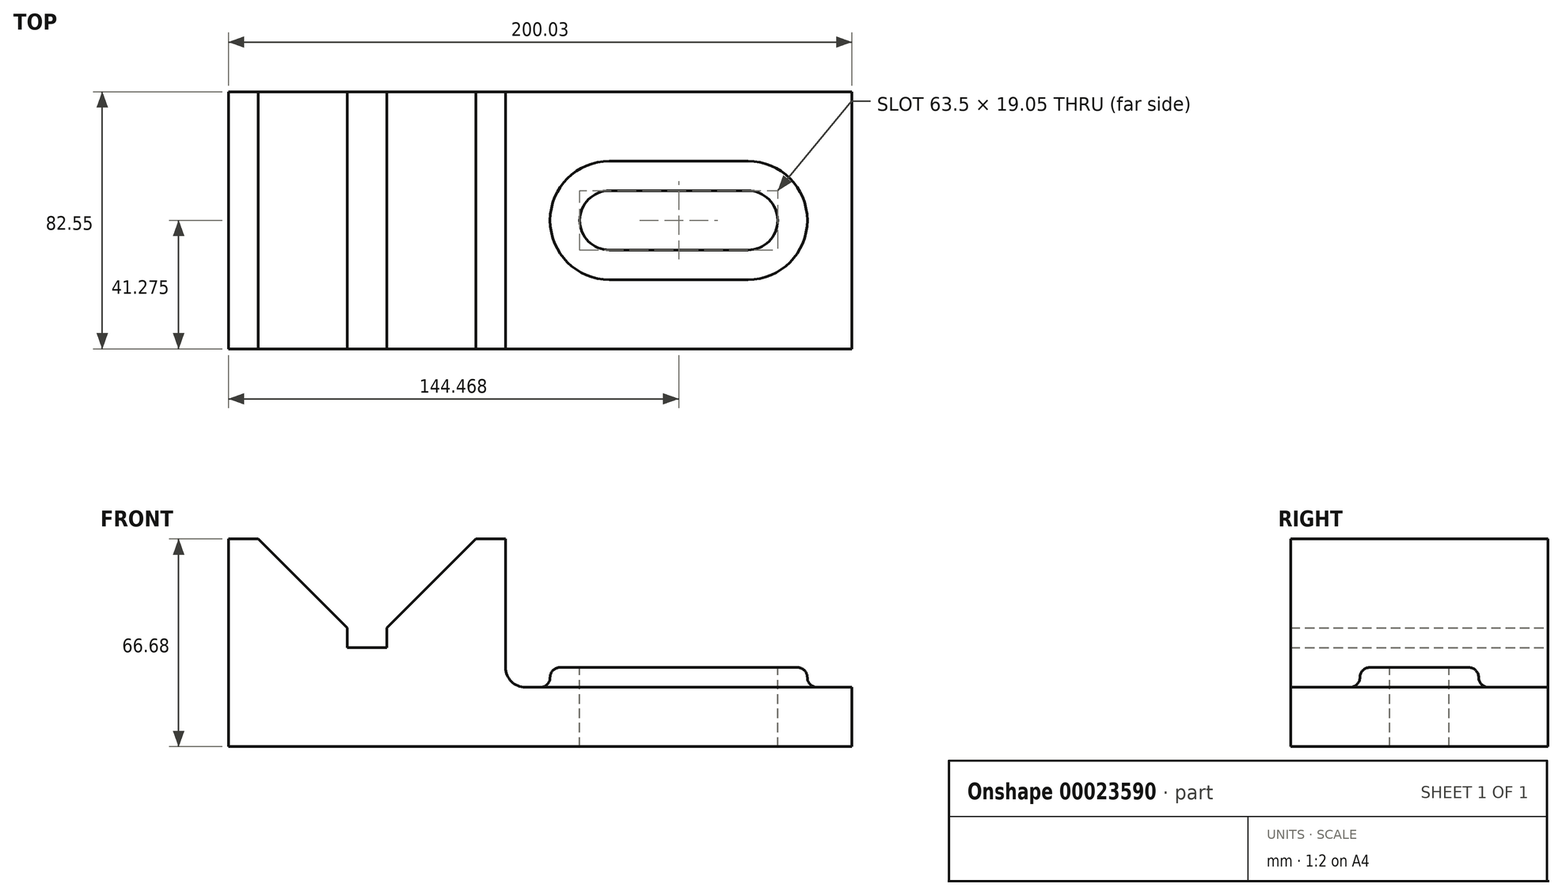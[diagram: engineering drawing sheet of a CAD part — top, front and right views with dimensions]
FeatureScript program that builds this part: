
annotation { "Feature Type Name" : "Feature", "Feature Type Description" : "" }
export const myFeature = defineFeature(function(context is Context, id is Id, definition is map)
    precondition{}
    {
        {
            var Q0;
            Q0=qCreatedBy(makeId("Front.planeOp"),FACE);
            var sketch = newSketch(context, id + "F0", { "sketchPlane" : qUnion([Q0])});
            skLineSegment(sketch, "E0.bottom", {"start": v(-200.03, 19.05) * mm, "end": v(0, 19.05) * mm});
            skLineSegment(sketch, "E0.top", {"start": v(-200.03, 0) * mm, "end": v(0, 0) * mm});
            skLineSegment(sketch, "E0.left", {"start": v(-200.03, 19.05) * mm, "end": v(-200.03, 0) * mm});
            skLineSegment(sketch, "E0.right", {"start": v(0, 19.05) * mm, "end": v(0, 0) * mm});
            skLineSegment(sketch, "E1.bottom", {"start": v(-200.03, 0) * mm, "end": v(-111.13, 0) * mm});
            skLineSegment(sketch, "E1.top", {"start": v(-200.03, 66.68) * mm, "end": v(-111.13, 66.68) * mm});
            skLineSegment(sketch, "E1.left", {"start": v(-200.03, 0) * mm, "end": v(-200.03, 66.68) * mm});
            skLineSegment(sketch, "E1.right", {"start": v(-111.13, 0) * mm, "end": v(-111.13, 66.68) * mm});
            skLineSegment(sketch, "E2", {"start": v(-190.5, 66.67) * mm, "end": v(-161.93, 38.1) * mm});
            skLineSegment(sketch, "E3", {"start": v(-161.93, 38.1) * mm, "end": v(-161.93, 31.75) * mm});
            skLineSegment(sketch, "E4", {"start": v(-161.93, 31.75) * mm, "end": v(-149.23, 31.75) * mm});
            skLineSegment(sketch, "E5", {"start": v(-149.23, 31.75) * mm, "end": v(-149.23, 38.1) * mm});
            skLineSegment(sketch, "E6", {"start": v(-149.23, 38.1) * mm, "end": v(-120.65, 66.68) * mm});
            skSolve(sketch);
        }
        {
            var Q0;
            {var subQ3=sQuery(id+"F0.wireOp",EDGE,"E0.top");Q0=makeQuery(id+"F0.imprint","IMPRINT",FACE,{"disambiguationData":[TD([[makeQuery(id+"F0.imprint","IMPRINT",EDGE,{"derivedFrom":subQ3}),1.0]])]});}
            var Q1;
            {var subQ3=sQuery(id+"F0.wireOp",EDGE,"E1.bottom");Q1=makeQuery(id+"F0.imprint","IMPRINT",FACE,{"disambiguationData":[TD([[makeQuery(id+"F0.imprint","IMPRINT",EDGE,{"derivedFrom":subQ3}),1.0]])]});}
            var Q2;
            {var subQ0=sQuery(id+"F0.wireOp",EDGE,"E2");Q2=makeQuery(id+"F0.imprint","IMPRINT",FACE,{"disambiguationData":[TD([[makeQuery(id+"F0.imprint","IMPRINT",EDGE,{"derivedFrom":subQ0}),-1.0]])]});}
            extrude(context, id + "F1", {"entities" : qUnion([Q0, Q1, Q2]), "depth" : 82.55 * mm});
        }
        {
            var Q0;
            Q0=makeQuery(id+"F1.opExtrude","SWEPT_FACE",FACE,{"disambiguationData":[OSD([sQuery(id+"F0.wireOp",EDGE,"E0.bottom")])]});
            var sketch = newSketch(context, id + "F2", { "sketchPlane" : qUnion([Q0])});
            skLineSegment(sketch, "E7.bottom", {"start": v(-77.79, -31.75) * mm, "end": v(-33.34, -31.75) * mm});
            skLineSegment(sketch, "E7.top", {"start": v(-77.79, -50.8) * mm, "end": v(-33.34, -50.8) * mm});
            skLineSegment(sketch, "E7.left", {"start": v(-77.79, -31.75) * mm, "end": v(-77.79, -50.8) * mm});
            skLineSegment(sketch, "E7.right", {"start": v(-33.34, -31.75) * mm, "end": v(-33.34, -50.8) * mm});
            skCircle(sketch, "E8", {"center": v(-77.79, -41.28) * mm, "radius": 9.53 * mm});
            skCircle(sketch, "E9", {"center": v(-33.34, -41.28) * mm, "radius": 9.53 * mm});
            skLineSegment(sketch, "E10", {"start": v(-55.56, 0) * mm, "end": v(-55.56, -31.75) * mm, "construction": true});
            skLineSegment(sketch, "E11", {"start": v(0, -41.28) * mm, "end": v(-66.68, -41.28) * mm, "construction": true});
            skSolve(sketch);
        }
        {
            var Q0;
            {var subQ1=sQuery(id+"F2.wireOp",EDGE,"E7.left");Q0=makeQuery(id+"F2.imprint","IMPRINT",FACE,{"disambiguationData":[TD([[makeQuery(id+"F2.imprint","IMPRINT",EDGE,{"derivedFrom":subQ1}),1.0]])]});}
            var Q1;
            {var subQ1=sQuery(id+"F2.wireOp",EDGE,"E7.left");Q1=makeQuery(id+"F2.imprint","IMPRINT",FACE,{"disambiguationData":[TD([[makeQuery(id+"F2.imprint","IMPRINT",EDGE,{"derivedFrom":subQ1}),-1.0]])]});}
            var Q2;
            {var subQ3=sQuery(id+"F2.wireOp",EDGE,"E7.bottom");Q2=makeQuery(id+"F2.imprint","IMPRINT",FACE,{"disambiguationData":[TD([[makeQuery(id+"F2.imprint","IMPRINT",EDGE,{"derivedFrom":subQ3}),-1.0]])]});}
            var Q3;
            {var subQ1=sQuery(id+"F2.wireOp",EDGE,"E7.right");Q3=makeQuery(id+"F2.imprint","IMPRINT",FACE,{"disambiguationData":[TD([[makeQuery(id+"F2.imprint","IMPRINT",EDGE,{"derivedFrom":subQ1}),-1.0]])]});}
            var Q4;
            {var subQ1=sQuery(id+"F2.wireOp",EDGE,"E7.right");Q4=makeQuery(id+"F2.imprint","IMPRINT",FACE,{"disambiguationData":[TD([[makeQuery(id+"F2.imprint","IMPRINT",EDGE,{"derivedFrom":subQ1}),1.0]])]});}
            extrude(context, id + "F3", {"entities" : qUnion([Q0, Q1, Q2, Q3, Q4]), "operationType" : NewBodyOperationType.REMOVE, "endBound" : BoundingType.THROUGH_ALL, "oppositeDirection" : true, "depth" : 25.4 * mm});
        }
        {
            var Q0;
            Q0=makeQuery(id+"F1.opExtrude","SWEPT_FACE",FACE,{"disambiguationData":[OSD([sQuery(id+"F0.wireOp",EDGE,"E0.bottom")])]});
            var sketch = newSketch(context, id + "F4", { "sketchPlane" : qUnion([Q0])});
            skLineSegment(sketch, "E12.0", {"start": v(-77.79, -22.23) * mm, "end": v(-33.34, -22.23) * mm});
            skArc(sketch, "E12.1", {"start": v(-77.79, -22.23) * mm, "mid": v(-96.84, -41.28) * mm, "end": v(-77.79, -60.33) * mm});
            skLineSegment(sketch, "E12.2", {"start": v(-77.79, -60.33) * mm, "end": v(-33.34, -60.33) * mm});
            skArc(sketch, "E12.3", {"start": v(-33.34, -60.33) * mm, "mid": v(-14.29, -41.28) * mm, "end": v(-33.34, -22.23) * mm});
            skSolve(sketch);
        }
        {
            var Q0;
            Q0 = qSketchRegion(id + "F4", true);
            extrude(context, id + "F5", {"entities" : qUnion([Q0]), "operationType" : NewBodyOperationType.ADD, "depth" : 6.35 * mm});
        }
        {
            var Q0;
            Q0=makeQuery(id+"F5.opExtrude","SWEPT_FACE",FACE,{"disambiguationData":[OSD([sQuery(id+"F4.wireOp",EDGE,"E12.1")])]});
            var Q1;
            Q1=makeQuery(id+"F5.opExtrude","SWEPT_FACE",FACE,{"disambiguationData":[OSD([sQuery(id+"F4.wireOp",EDGE,"E12.2")])]});
            var Q2;
            Q2=makeQuery(id+"F5.opExtrude","SWEPT_FACE",FACE,{"disambiguationData":[OSD([sQuery(id+"F4.wireOp",EDGE,"E12.3")])]});
            var Q3;
            Q3=makeQuery(id+"F5.opExtrude","SWEPT_FACE",FACE,{"disambiguationData":[OSD([sQuery(id+"F4.wireOp",EDGE,"E12.0")])]});
            fillet(context, id + "F6", {"entities" : qUnion([Q0, Q1, Q2, Q3]), "radius" : 3.17 * mm, "tangentPropagation" : true, "allowEdgeOverflow" : false});
        }
        {
            var Q0;
            Q0=makeQuery(id+"F1.opExtrude","SWEPT_EDGE",EDGE,{"disambiguationData":[OSD([sQuery(id+"F0.wireOp",EDGE,"E0.bottom"),sQuery(id+"F0.wireOp",EDGE,"E1.right")])]});
            fillet(context, id + "F7", {"entities" : qUnion([Q0]), "radius" : 6.35 * mm, "tangentPropagation" : true, "allowEdgeOverflow" : false});
        }
        {
            var Q0;
            Q0=makeQuery(id+"F1.opExtrude","SWEPT_FACE",FACE,{"disambiguationData":[OSD([sQuery(id+"F0.wireOp",EDGE,"E0.top"),sQuery(id+"F0.wireOp",EDGE,"E1.bottom")])]});
            var sketch = newSketch(context, id + "F8", { "sketchPlane" : qUnion([Q0])});
            skSolve(sketch);
        }
        {
            var Q0;
            Q0 = qSketchRegion(id + "F8", true);
            var Q1;
            {var subQ0=makeQuery(id+"F1.opExtrude","SWEPT_FACE",FACE,{"disambiguationData":[OSD([sQuery(id+"F0.wireOp",EDGE,"E0.top"),sQuery(id+"F0.wireOp",EDGE,"E1.bottom")])]});Q1=makeQuery(id+"F8.imprint","IMPRINT",FACE,{"disambiguationData":[TD([[makeQuery(id+"F8.imprint","IMPRINT",EDGE,{"derivedFrom":makeQuery(id+"F3.boolean.opBoolean","INTERSECT",EDGE,{"derivedFrom":[subQ0,makeQuery(id+"F3.opExtrude","SWEPT_FACE",FACE,{"disambiguationData":[OSD([sQuery(id+"F2.wireOp",EDGE,"E7.bottom")])]})]})}),1.0]])]});}
            extrude(context, id + "F9", {"entities" : qUnion([Q0, Q1]), "operationType" : NewBodyOperationType.REMOVE, "endBound" : BoundingType.THROUGH_ALL, "oppositeDirection" : true, "depth" : 25.4 * mm});
        }
    });
